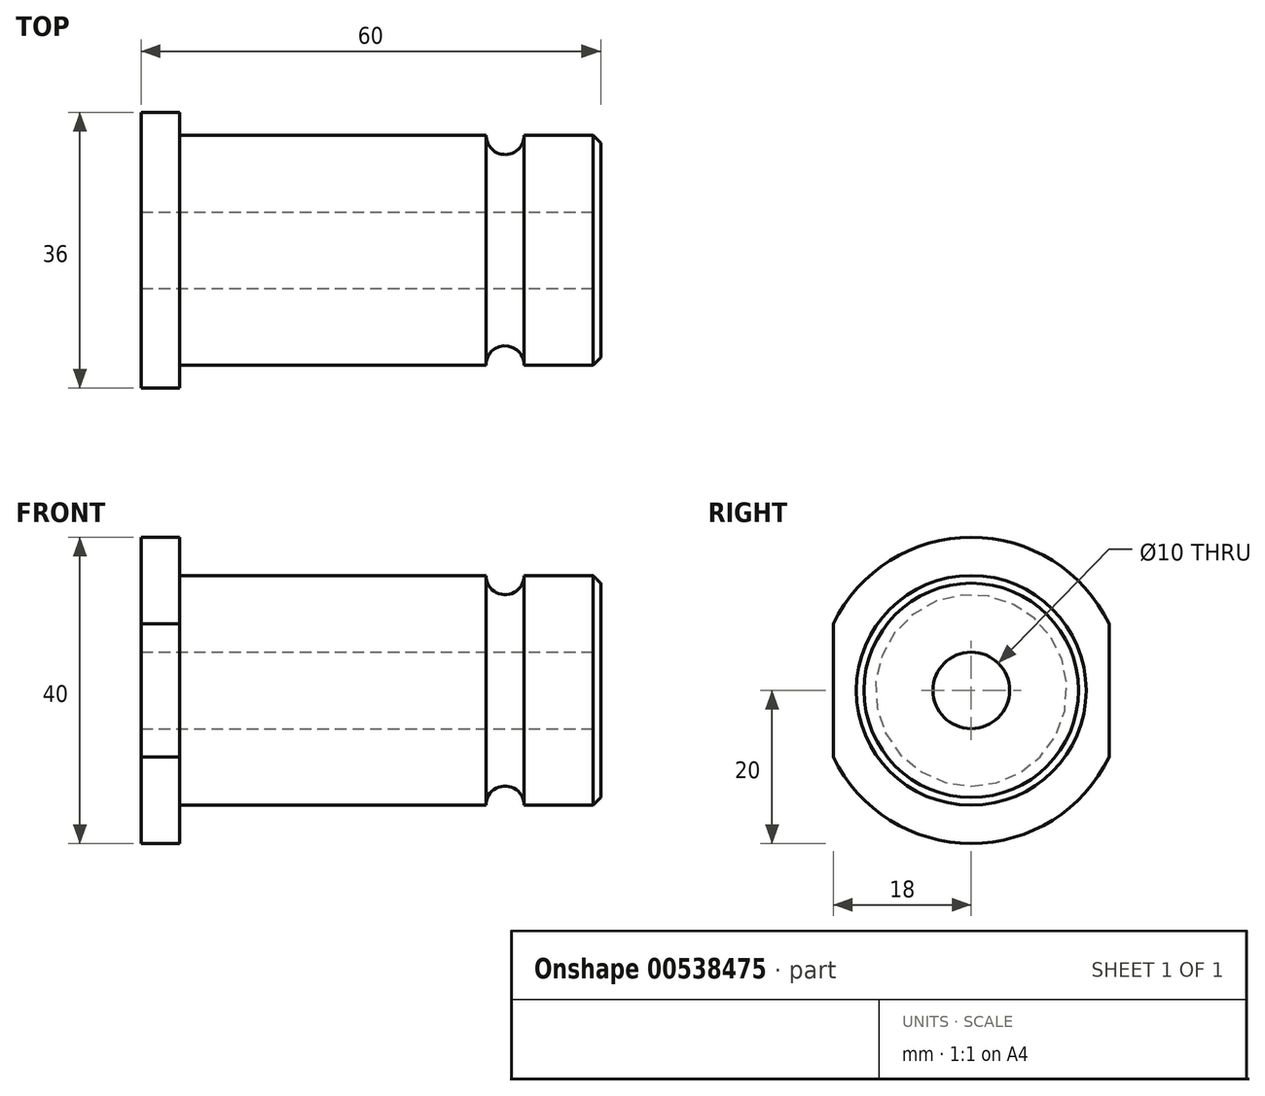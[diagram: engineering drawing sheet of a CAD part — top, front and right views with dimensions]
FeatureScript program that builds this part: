
annotation { "Feature Type Name" : "Feature", "Feature Type Description" : "" }
export const myFeature = defineFeature(function(context is Context, id is Id, definition is map)
    precondition{}
    {
        {
            var Q0;
            Q0=qCreatedBy(makeId("Front.planeOp"),FACE);
            var sketch = newSketch(context, id + "F0", { "sketchPlane" : qUnion([Q0])});
            skLineSegment(sketch, "E0", {"start": v(0, 0) * mm, "end": v(0, 20) * mm});
            skLineSegment(sketch, "E1", {"start": v(0, 20) * mm, "end": v(5, 20) * mm});
            skLineSegment(sketch, "E2", {"start": v(5, 20) * mm, "end": v(5, 15) * mm});
            skLineSegment(sketch, "E3", {"start": v(5, 15) * mm, "end": v(60, 15) * mm});
            skLineSegment(sketch, "E4", {"start": v(60, 15) * mm, "end": v(60, 0) * mm});
            skLineSegment(sketch, "E5", {"start": v(60, 0) * mm, "end": v(0, 0) * mm});
            skSolve(sketch);
        }
        {
            var Q0;
            Q0=makeQuery(id+"F0.imprint","IMPRINT",FACE,{"disambiguationData":[TD([[makeQuery(id+"F0.imprint","IMPRINT",EDGE,{"derivedFrom":sQuery(id+"F0.wireOp",EDGE,"E0")}),-1.0]])]});
            var Q1;
            Q1=sQuery(id+"F0.wireOp",EDGE,"E5");
            revolve(context, id + "F1", {"entities" : qUnion([Q0]), "axis" : qUnion([Q1]), "revolveType" : RevolveType.FULL});
        }
        {
            var Q0;
            Q0=qCreatedBy(makeId("Front.planeOp"),FACE);
            var sketch = newSketch(context, id + "F2", { "sketchPlane" : qUnion([Q0])});
            skCircle(sketch, "E6", {"center": v(47.5, 15) * mm, "radius": 2.5 * mm});
            skSolve(sketch);
        }
        {
            var Q0;
            Q0=qSketchRegion(id+"F2",true);
            var Q1;
            Q1=makeQuery(id+"F1.opRevolve","SWEPT_FACE",FACE,{"disambiguationData":[OSD([sQuery(id+"F0.wireOp",EDGE,"E3")])]});
            revolve(context, id + "F3", {"operationType" : NewBodyOperationType.REMOVE, "entities" : qUnion([Q0]), "axis" : qUnion([Q1]), "revolveType" : RevolveType.FULL, "oppositeDirection" : true});
        }
        {
            var Q0;
            Q0=makeQuery(id+"F1.opRevolve","SWEPT_EDGE",EDGE,{"disambiguationData":[OSD([sQuery(id+"F0.wireOp",EDGE,"E3"),sQuery(id+"F0.wireOp",EDGE,"E4")])]});
            chamfer(context, id + "F4", {"entities" : qUnion([Q0]), "width" : 1 * mm, "tangentPropagation" : true});
        }
        {
            var Q0;
            Q0=makeQuery(id+"F1.opRevolve","SWEPT_FACE",FACE,{"disambiguationData":[OSD([sQuery(id+"F0.wireOp",EDGE,"E4")])]});
            var sketch = newSketch(context, id + "F5", { "sketchPlane" : qUnion([Q0])});
            skCircle(sketch, "E7", {"center": v(0, 0) * mm, "radius": 5 * mm});
            skSolve(sketch);
        }
        {
            var Q0;
            Q0=qSketchRegion(id+"F5",true);
            extrude(context, id + "F6", {"entities" : qUnion([Q0]), "operationType" : NewBodyOperationType.REMOVE, "endBound" : BoundingType.THROUGH_ALL, "oppositeDirection" : true, "depth" : 25 * mm, "offsetDistance" : 25 * mm});
        }
        {
            var Q0;
            Q0=makeQuery(id+"F1.opRevolve","SWEPT_FACE",FACE,{"disambiguationData":[OSD([sQuery(id+"F0.wireOp",EDGE,"E0")])]});
            var sketch = newSketch(context, id + "F7", { "sketchPlane" : qUnion([Q0])});
            skLineSegment(sketch, "E8.bottom", {"start": v(18, -20) * mm, "end": v(-18, -20) * mm});
            skLineSegment(sketch, "E8.top", {"start": v(18, 20) * mm, "end": v(-18, 20) * mm});
            skLineSegment(sketch, "E8.left", {"start": v(18, -20) * mm, "end": v(18, 20) * mm});
            skLineSegment(sketch, "E8.right", {"start": v(-18, -20) * mm, "end": v(-18, 20) * mm});
            skPoint(sketch, "E8.middle", {"position": v(0, 0) * mm});
            skSolve(sketch);
        }
        {
            var Q0;
            {var subQ0=sQuery(id+"F7.wireOp",EDGE,"E8.right");var subQ1=makeQuery(id+"F1.opRevolve","SWEPT_EDGE",EDGE,{"disambiguationData":[OSD([sQuery(id+"F0.wireOp",EDGE,"E0"),sQuery(id+"F0.wireOp",EDGE,"E1")])]});var subQ2=makeQuery(id+"F7.imprint","INTERSECT",VERTEX,{"disambiguationData":[OD(0.0)],"derivedFrom":[subQ1,subQ0]});Q0=makeQuery(id+"F7.imprint","IMPRINT",FACE,{"disambiguationData":[TD([[makeQuery(id+"F7.imprint","IMPRINT",EDGE,{"disambiguationData":[TD([[subQ2,-1.0]])],"derivedFrom":subQ0}),1.0]])]});}
            var Q1;
            {var subQ0=sQuery(id+"F7.wireOp",EDGE,"E8.left");var subQ1=makeQuery(id+"F1.opRevolve","SWEPT_EDGE",EDGE,{"disambiguationData":[OSD([sQuery(id+"F0.wireOp",EDGE,"E0"),sQuery(id+"F0.wireOp",EDGE,"E1")])]});var subQ2=makeQuery(id+"F7.imprint","INTERSECT",VERTEX,{"disambiguationData":[OD(0.0)],"derivedFrom":[subQ1,subQ0]});Q1=makeQuery(id+"F7.imprint","IMPRINT",FACE,{"disambiguationData":[TD([[makeQuery(id+"F7.imprint","IMPRINT",EDGE,{"disambiguationData":[TD([[subQ2,-1.0]])],"derivedFrom":subQ0}),-1.0]])]});}
            extrude(context, id + "F8", {"entities" : qUnion([Q0, Q1]), "operationType" : NewBodyOperationType.REMOVE, "endBound" : BoundingType.UP_TO_NEXT, "oppositeDirection" : true, "depth" : 25 * mm, "offsetDistance" : 25 * mm});
        }
    });
